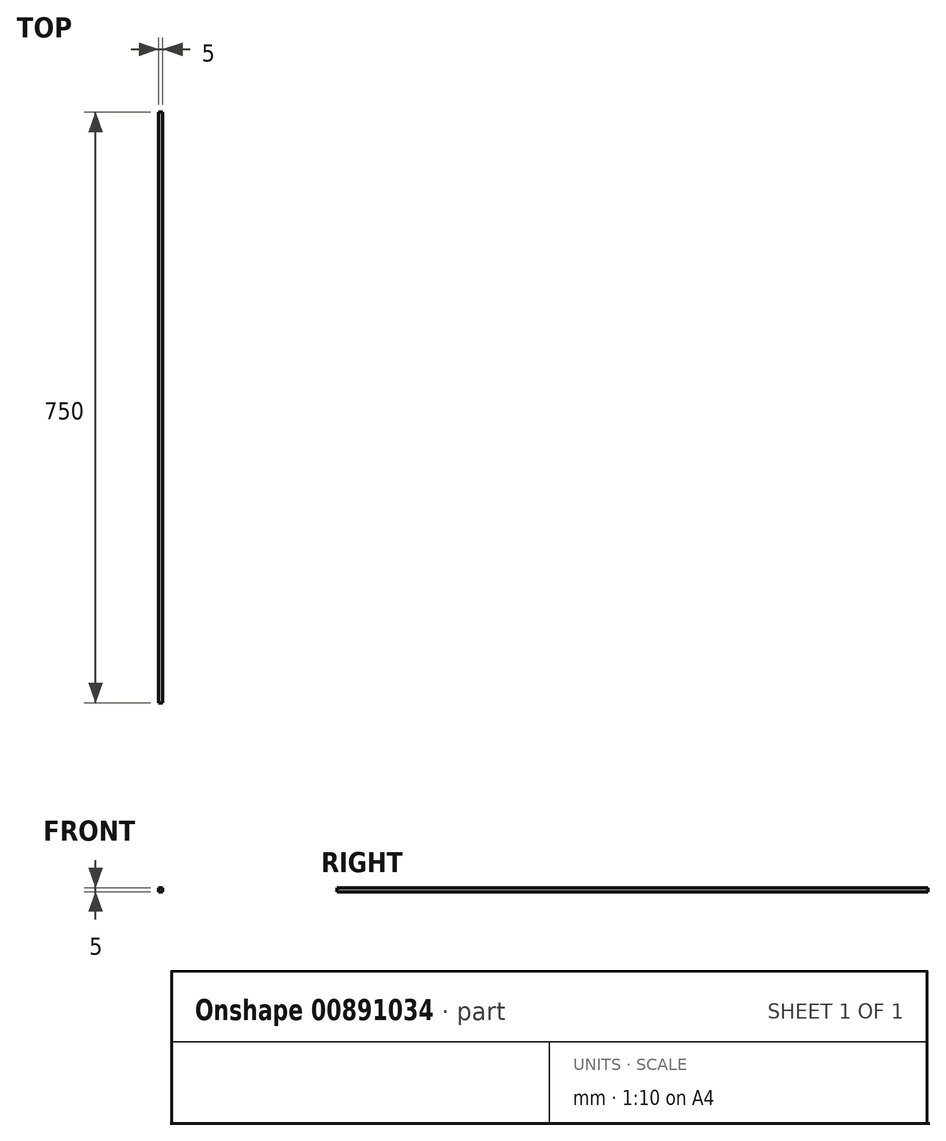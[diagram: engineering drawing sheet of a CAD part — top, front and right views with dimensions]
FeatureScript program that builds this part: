
annotation { "Feature Type Name" : "Feature", "Feature Type Description" : "" }
export const myFeature = defineFeature(function(context is Context, id is Id, definition is map)
    precondition{}
    {
        {
            var Q0;
            Q0=qCreatedBy(makeId("Front.planeOp"),FACE);
            var sketch = newSketch(context, id + "F0", { "sketchPlane" : qUnion([Q0])});
            skLineSegment(sketch, "E0.bottom", {"start": v(2.5, 0) * mm, "end": v(-2.5, 0) * mm});
            skLineSegment(sketch, "E0.top", {"start": v(2.5, -5) * mm, "end": v(-2.5, -5) * mm});
            skLineSegment(sketch, "E0.left", {"start": v(2.5, 0) * mm, "end": v(2.5, -5) * mm});
            skLineSegment(sketch, "E0.right", {"start": v(-2.5, 0) * mm, "end": v(-2.5, -5) * mm});
            skPoint(sketch, "E0.middle", {"position": v(0, -2.5) * mm});
            skSolve(sketch);
        }
        {
            var Q0;
            Q0 = qSketchRegion(id + "F0", true);
            extrude(context, id + "F1", {"entities" : qUnion([Q0]), "depth" : 750 * mm, "offsetDistance" : 25 * mm});
        }
    });
